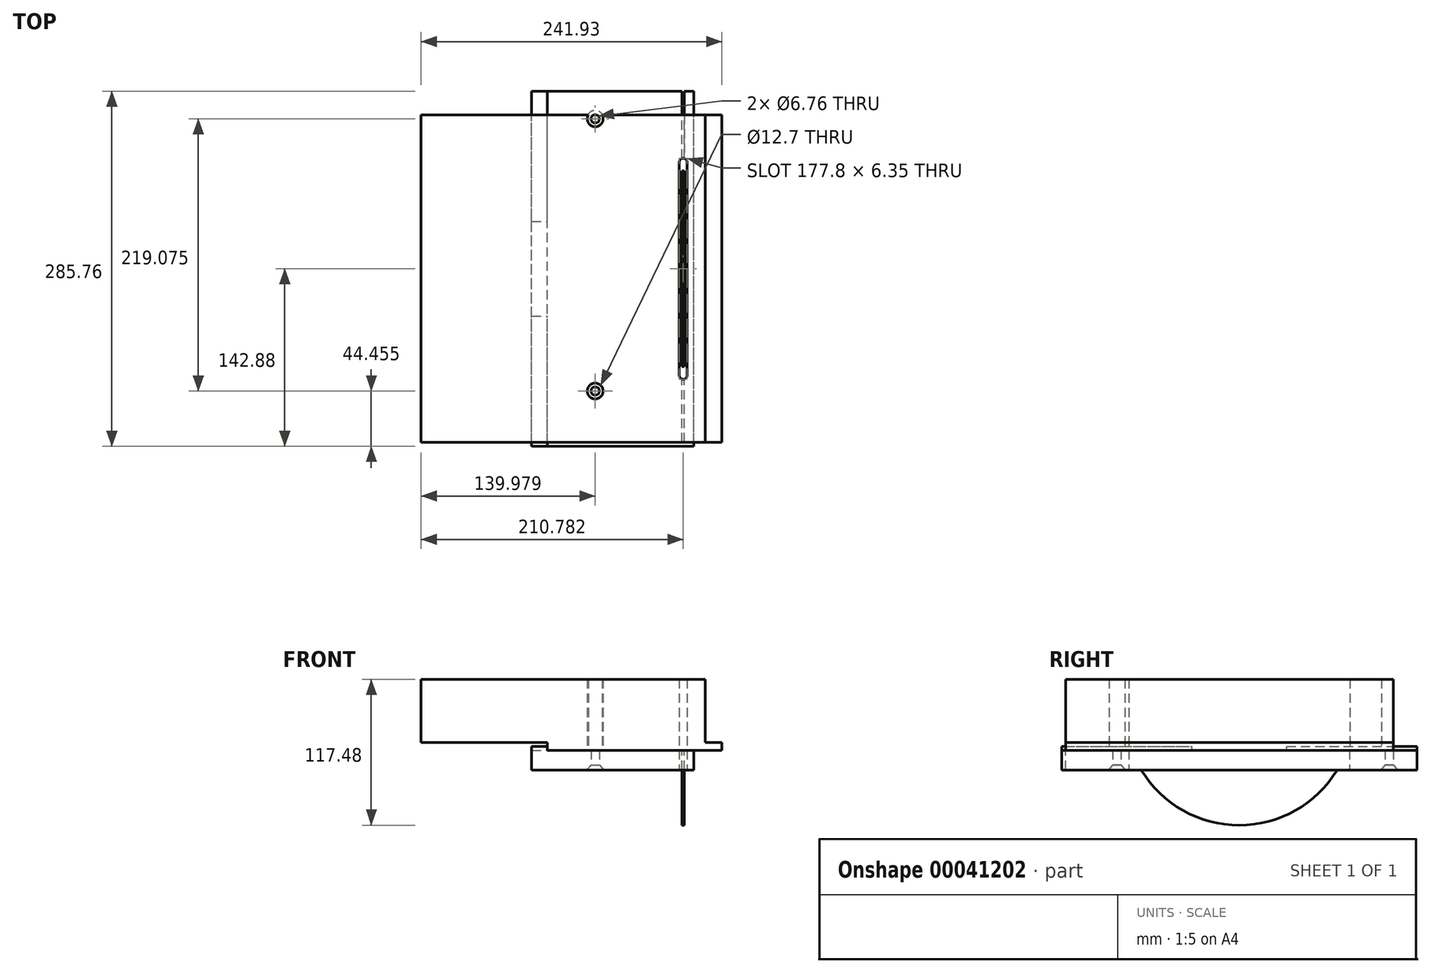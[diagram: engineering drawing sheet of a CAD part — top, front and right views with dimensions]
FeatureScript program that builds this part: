
annotation { "Feature Type Name" : "Feature", "Feature Type Description" : "" }
export const myFeature = defineFeature(function(context is Context, id is Id, definition is map)
    precondition{}
    {
        {
            var Q0;
            Q0=qCreatedBy(makeId("Front.planeOp"),FACE);
            var sketch = newSketch(context, id + "F0", { "sketchPlane" : qUnion([Q0])});
            skLineSegment(sketch, "E0.bottom", {"start": v(0, 0) * mm, "end": v(140.34, 0) * mm});
            skLineSegment(sketch, "E0.top", {"start": v(0, 6.35) * mm, "end": v(140.34, 6.35) * mm});
            skLineSegment(sketch, "E0.left", {"start": v(0, 0) * mm, "end": v(0, 6.35) * mm});
            skLineSegment(sketch, "E0.right", {"start": v(140.34, 0) * mm, "end": v(140.34, 6.35) * mm});
            skLineSegment(sketch, "E1.bottom", {"start": v(127, 6.35) * mm, "end": v(-101.6, 6.35) * mm});
            skLineSegment(sketch, "E1.top", {"start": v(127, 57.15) * mm, "end": v(-101.6, 57.15) * mm});
            skLineSegment(sketch, "E1.left", {"start": v(127, 6.35) * mm, "end": v(127, 57.15) * mm});
            skLineSegment(sketch, "E1.right", {"start": v(-101.6, 6.35) * mm, "end": v(-101.6, 57.15) * mm});
            skLineSegment(sketch, "E2.bottom", {"start": v(108.23, 0) * mm, "end": v(110.13, 0) * mm});
            skLineSegment(sketch, "E2.top", {"start": v(108.23, -60.96) * mm, "end": v(110.13, -60.96) * mm});
            skLineSegment(sketch, "E2.left", {"start": v(108.23, 0) * mm, "end": v(108.23, -60.96) * mm});
            skLineSegment(sketch, "E2.right", {"start": v(110.13, 0) * mm, "end": v(110.13, -60.96) * mm});
            skSolve(sketch);
        }
        {
            var Q0;
            Q0 = qSketchRegion(id + "F0", true);
            extrude(context, id + "F1", {"entities" : qUnion([Q0]), "depth" : 139.7 * mm, "hasSecondDirection" : true, "secondDirectionOppositeDirection" : true, "secondDirectionDepth" : 123.82 * mm});
        }
        {
            var Q0;
            Q0=qCreatedBy(makeId("Front.planeOp"),FACE);
            var sketch = newSketch(context, id + "F2", { "sketchPlane" : qUnion([Q0])});
            skLineSegment(sketch, "E3.bottom", {"start": v(0, 0) * mm, "end": v(117.75, 0) * mm});
            skLineSegment(sketch, "E3.top", {"start": v(0, -15.88) * mm, "end": v(117.75, -15.88) * mm});
            skLineSegment(sketch, "E3.left", {"start": v(0, 0) * mm, "end": v(0, -15.88) * mm});
            skLineSegment(sketch, "E3.right", {"start": v(117.75, 0) * mm, "end": v(117.75, -15.88) * mm});
            skLineSegment(sketch, "E4.bottom", {"start": v(0, -15.88) * mm, "end": v(-12.7, -15.88) * mm});
            skLineSegment(sketch, "E4.top", {"start": v(0, 3.18) * mm, "end": v(-12.7, 3.17) * mm});
            skLineSegment(sketch, "E4.left", {"start": v(0, -15.88) * mm, "end": v(0, 3.18) * mm});
            skLineSegment(sketch, "E4.right", {"start": v(-12.7, -15.88) * mm, "end": v(-12.7, 3.17) * mm});
            skSolve(sketch);
        }
        {
            var Q0;
            Q0=makeQuery(id+"F2.imprint","IMPRINT",FACE,{"disambiguationData":[TD([[makeQuery(id+"F2.imprint","IMPRINT",EDGE,{"derivedFrom":sQuery(id+"F2.wireOp",EDGE,"E3.bottom")}),-1.0]])]});
            var Q1;
            {var subQ3=sQuery(id+"F2.wireOp",EDGE,"E4.bottom");Q1=makeQuery(id+"F2.imprint","IMPRINT",FACE,{"disambiguationData":[TD([[makeQuery(id+"F2.imprint","IMPRINT",EDGE,{"derivedFrom":subQ3}),-1.0]])]});}
            var Q2;
            Q2=makeQuery(id+"F1.opExtrude","CAP_FACE",FACE,{"disambiguationData":[OSD([sQuery(id+"F0.wireOp",EDGE,"E0.bottom"),sQuery(id+"F0.wireOp",EDGE,"E0.top"),sQuery(id+"F0.wireOp",EDGE,"E0.left"),sQuery(id+"F0.wireOp",EDGE,"E0.right"),sQuery(id+"F0.wireOp",EDGE,"E1.bottom"),sQuery(id+"F0.wireOp",EDGE,"E1.top"),sQuery(id+"F0.wireOp",EDGE,"E1.left"),sQuery(id+"F0.wireOp",EDGE,"E1.right"),sQuery(id+"F0.wireOp",EDGE,"E2.top"),sQuery(id+"F0.wireOp",EDGE,"E2.left"),sQuery(id+"F0.wireOp",EDGE,"E2.right")])],"isStart":true});
            extrude(context, id + "F3", {"entities" : qUnion([Q0, Q1]), "depth" : 142.88 * mm, "hasSecondDirection" : true, "secondDirectionOppositeDirection" : true, "secondDirectionBoundEntityFace" : qUnion([Q2]), "secondDirectionDepth" : 142.88 * mm});
        }
        {
            var Q0;
            Q0=makeQuery(id+"F3.opExtrude","SWEPT_FACE",FACE,{"disambiguationData":[OSD([sQuery(id+"F2.wireOp",EDGE,"E3.top")])]});
            var sketch = newSketch(context, id + "F4", { "sketchPlane" : qUnion([Q0])});
            skLineSegment(sketch, "E5.bottom", {"start": v(109.18, -88.9) * mm, "end": v(109.18, -88.9) * mm});
            skLineSegment(sketch, "E5.top", {"start": v(109.18, 88.9) * mm, "end": v(109.18, 88.9) * mm});
            skLineSegment(sketch, "E5.left", {"start": v(112.36, 85.73) * mm, "end": v(112.36, -85.73) * mm});
            skLineSegment(sketch, "E5.right", {"start": v(106, 85.73) * mm, "end": v(106, -85.73) * mm});
            skArc(sketch, "E6.filletArc", {"start": v(109.18, 88.9) * mm, "mid": v(106.94, 87.97) * mm, "end": v(106, 85.73) * mm});
            skArc(sketch, "E7.filletArc", {"start": v(112.36, 85.73) * mm, "mid": v(111.43, 87.97) * mm, "end": v(109.18, 88.9) * mm});
            skArc(sketch, "E8.filletArc", {"start": v(109.18, -88.9) * mm, "mid": v(111.43, -87.97) * mm, "end": v(112.36, -85.73) * mm});
            skArc(sketch, "E9.filletArc", {"start": v(106, -85.73) * mm, "mid": v(106.94, -87.97) * mm, "end": v(109.18, -88.9) * mm});
            skSolve(sketch);
        }
        {
            var Q0;
            Q0=makeQuery(id+"F1.opExtrude","SWEPT_FACE",FACE,{"disambiguationData":[OSD([sQuery(id+"F0.wireOp",EDGE,"E2.right")])]});
            var sketch = newSketch(context, id + "F5", { "sketchPlane" : qUnion([Q0])});
            skLineSegment(sketch, "E10.0", {"start": v(-139.7, 0) * mm, "end": v(-139.7, -60.96) * mm});
            skLineSegment(sketch, "E11.0", {"start": v(123.83, 0) * mm, "end": v(123.83, -60.96) * mm});
            skLineSegment(sketch, "E12", {"start": v(0, 0) * mm, "end": v(0, 82.53) * mm, "construction": true});
            skLineSegment(sketch, "E13", {"start": v(-86.43, 0) * mm, "end": v(-139.7, 0) * mm});
            skLineSegment(sketch, "E14", {"start": v(-139.7, 0) * mm, "end": v(-139.7, -88.9) * mm});
            skLineSegment(sketch, "E15", {"start": v(-139.7, -88.9) * mm, "end": v(152.4, -88.9) * mm});
            skLineSegment(sketch, "E16", {"start": v(152.4, -88.9) * mm, "end": v(152.4, 0) * mm});
            skLineSegment(sketch, "E17", {"start": v(152.4, 0) * mm, "end": v(86.43, 0) * mm});
            skArc(sketch, "E18.converted", {"start": v(-86.43, 0) * mm, "mid": v(0, -60.33) * mm, "end": v(86.43, 0) * mm});
            skSolve(sketch);
        }
        {
            var Q0;
            Q0 = qSketchRegion(id + "F5", true);
            var Q1;
            Q1=makeQuery(id+"F1.opExtrude","SWEPT_FACE",FACE,{"disambiguationData":[OSD([sQuery(id+"F0.wireOp",EDGE,"E2.left")])]});
            extrude(context, id + "F6", {"entities" : qUnion([Q0]), "operationType" : NewBodyOperationType.REMOVE, "endBound" : BoundingType.UP_TO_SURFACE, "oppositeDirection" : true, "endBoundEntityFace" : qUnion([Q1]), "depth" : 5.08 * mm});
        }
        {
            var Q0;
            {var subQ0=sQuery(id+"F0.wireOp",EDGE,"E0.bottom");Q0=makeQuery(id+"F6.boolean.opBoolean","MERGE",FACE,{"derivedFrom":[makeQuery(id+"F1.opExtrude","SWEPT_FACE",FACE,{"disambiguationData":[OSD([subQ0]),TDD([makeQuery(id+"F0.imprint","IMPRINT",EDGE,{"disambiguationData":[TD([[makeQuery(id+"F0.imprint","INTERSECT",VERTEX,{"derivedFrom":[subQ0,sQuery(id+"F0.wireOp",EDGE,"E0.left")]}),-1.0]])],"derivedFrom":subQ0})])]}),makeQuery(id+"F1.opExtrude","SWEPT_FACE",FACE,{"disambiguationData":[OSD([subQ0]),TDD([makeQuery(id+"F0.imprint","IMPRINT",EDGE,{"disambiguationData":[TD([[makeQuery(id+"F0.imprint","INTERSECT",VERTEX,{"derivedFrom":[subQ0,sQuery(id+"F0.wireOp",EDGE,"E0.right")]}),1.0]])],"derivedFrom":subQ0})])]}),makeQuery(id+"F6.opExtrude","SWEPT_FACE",FACE,{"disambiguationData":[OSD([sQuery(id+"F5.wireOp",EDGE,"E13")])]}),makeQuery(id+"F6.opExtrude","SWEPT_FACE",FACE,{"disambiguationData":[OSD([sQuery(id+"F5.wireOp",EDGE,"E17")])]})]});}
            var sketch = newSketch(context, id + "F7", { "sketchPlane" : qUnion([Q0])});
            skCircle(sketch, "E19", {"center": v(38.38, -120.65) * mm, "radius": 6.35 * mm});
            skCircle(sketch, "E20", {"center": v(38.38, 98.43) * mm, "radius": 6.35 * mm});
            skSolve(sketch);
        }
        {
            var Q0;
            Q0 = qSketchRegion(id + "F7", true);
            var Q1;
            Q1=makeQuery(id+"F1.opExtrude","SWEPT_FACE",FACE,{"disambiguationData":[OSD([sQuery(id+"F0.wireOp",EDGE,"E1.top")])]});
            extrude(context, id + "F8", {"entities" : qUnion([Q0]), "operationType" : NewBodyOperationType.REMOVE, "endBound" : BoundingType.UP_TO_SURFACE, "oppositeDirection" : true, "endBoundEntityFace" : qUnion([Q1]), "depth" : 25.4 * mm});
        }
        {
            var Q0;
            Q0=makeQuery(id+"F7.imprint","IMPRINT",FACE,{"disambiguationData":[TD([[makeQuery(id+"F7.imprint","IMPRINT",EDGE,{"derivedFrom":sQuery(id+"F7.wireOp",EDGE,"E19")}),-1.0]])]});
            var sketch = newSketch(context, id + "F9", { "sketchPlane" : qUnion([Q0])});
            skPoint(sketch, "E21.0", {"position": v(38.38, 98.43) * mm});
            skPoint(sketch, "E22.0", {"position": v(38.38, -120.65) * mm});
            skSolve(sketch);
        }
        {
            var Q0;
            Q0=makeQuery(id+"F3.opExtrude","SWEPT_FACE",FACE,{"disambiguationData":[OSD([sQuery(id+"F2.wireOp",EDGE,"E3.top"),sQuery(id+"F2.wireOp",EDGE,"E4.bottom")])]});
            var sketch = newSketch(context, id + "F10", { "sketchPlane" : qUnion([Q0])});
            skPoint(sketch, "E23.0", {"position": v(38.38, -120.65) * mm});
            skPoint(sketch, "E24.0", {"position": v(38.38, 98.43) * mm});
            skSolve(sketch);
        }
        {
            var Q0;
            Q0=sQuery(id+"F10.wireOp",VERTEX,"E23.0");
            var Q1;
            Q1=sQuery(id+"F10.wireOp",VERTEX,"E24.0");
            var Q2;
            Q2=makeQuery(id+"F3.opExtrude","SWEPT_BODY",BODY,{"disambiguationData":[OSD([sQuery(id+"F2.wireOp",EDGE,"E3.bottom"),sQuery(id+"F2.wireOp",EDGE,"E3.top"),sQuery(id+"F2.wireOp",EDGE,"E3.right"),sQuery(id+"F2.wireOp",EDGE,"E4.bottom"),sQuery(id+"F2.wireOp",EDGE,"E4.top"),sQuery(id+"F2.wireOp",EDGE,"E4.left"),sQuery(id+"F2.wireOp",EDGE,"E4.right")])]});
            hole(context, id + "F11", {"style" : HoleStyle.C_SINK, "endStyle" : HoleEndStyle.THROUGH, "standardTappedOrClearance" : lookupTablePath({ "standard" : "ANSI", "fit" : "Normal (ASME)", "size" : "1/4", "type" : "Clearance" }), "standardBlindInLast" : lookupTablePath({ "fit" : "Free", "standard" : "ANSI", "size" : "1/4", "type" : "Clearance" }), "holeDiameter" : 6.76 * mm, "cSinkDiameter" : 13.5 * mm, "cSinkAngle" : 82 * degree, "locations" : qUnion([Q0, Q1]), "scope" : qUnion([Q2]), "isTappedThrough" : true});
        }
        {
            var Q0;
            Q0 = qSketchRegion(id + "F4", true);
            var Q1;
            Q1=makeQuery(id+"F1.opExtrude","SWEPT_BODY",BODY,{"disambiguationData":[OSD([sQuery(id+"F0.wireOp",EDGE,"E0.bottom"),sQuery(id+"F0.wireOp",EDGE,"E0.top"),sQuery(id+"F0.wireOp",EDGE,"E0.left"),sQuery(id+"F0.wireOp",EDGE,"E0.right"),sQuery(id+"F0.wireOp",EDGE,"E1.bottom"),sQuery(id+"F0.wireOp",EDGE,"E1.top"),sQuery(id+"F0.wireOp",EDGE,"E1.left"),sQuery(id+"F0.wireOp",EDGE,"E1.right"),sQuery(id+"F0.wireOp",EDGE,"E2.top"),sQuery(id+"F0.wireOp",EDGE,"E2.left"),sQuery(id+"F0.wireOp",EDGE,"E2.right")])]});
            extrude(context, id + "F12", {"entities" : qUnion([Q0]), "operationType" : NewBodyOperationType.REMOVE, "endBound" : BoundingType.UP_TO_BODY, "oppositeDirection" : true, "endBoundEntityBody" : qUnion([Q1]), "depth" : 25.4 * mm});
        }
        {
            var Q0;
            Q0=makeQuery(id+"F3.opExtrude","SWEPT_FACE",FACE,{"disambiguationData":[OSD([sQuery(id+"F2.wireOp",EDGE,"E4.left")])]});
            var sketch = newSketch(context, id + "F13", { "sketchPlane" : qUnion([Q0])});
            skLineSegment(sketch, "E25.bottom", {"start": v(0, 0) * mm, "end": v(38.1, 0) * mm});
            skLineSegment(sketch, "E25.top", {"start": v(0, 3.18) * mm, "end": v(38.1, 3.18) * mm});
            skLineSegment(sketch, "E25.right", {"start": v(38.1, 0) * mm, "end": v(38.1, 3.18) * mm});
            skLineSegment(sketch, "E26.MirrorCS", {"start": v(-38.1, 0) * mm, "end": v(-38.1, 3.18) * mm});
            skLineSegment(sketch, "E27.MirrorCS", {"start": v(0, 0) * mm, "end": v(-38.1, 0) * mm});
            skLineSegment(sketch, "E28.MirrorCS", {"start": v(0, 3.18) * mm, "end": v(-38.1, 3.18) * mm});
            skSolve(sketch);
        }
        {
            var Q0;
            Q0=makeQuery(id+"F13.imprint","IMPRINT",FACE,{"disambiguationData":[TD([[makeQuery(id+"F13.imprint","IMPRINT",EDGE,{"derivedFrom":sQuery(id+"F13.wireOp",EDGE,"E25.bottom")}),1.0]])]});
            var Q1;
            Q1=makeQuery(id+"F3.opExtrude","SWEPT_FACE",FACE,{"disambiguationData":[OSD([sQuery(id+"F2.wireOp",EDGE,"E4.right")])]});
            extrude(context, id + "F14", {"entities" : qUnion([Q0]), "operationType" : NewBodyOperationType.REMOVE, "endBound" : BoundingType.UP_TO_SURFACE, "oppositeDirection" : true, "endBoundEntityFace" : qUnion([Q1]), "depth" : 25.4 * mm});
        }
    });
